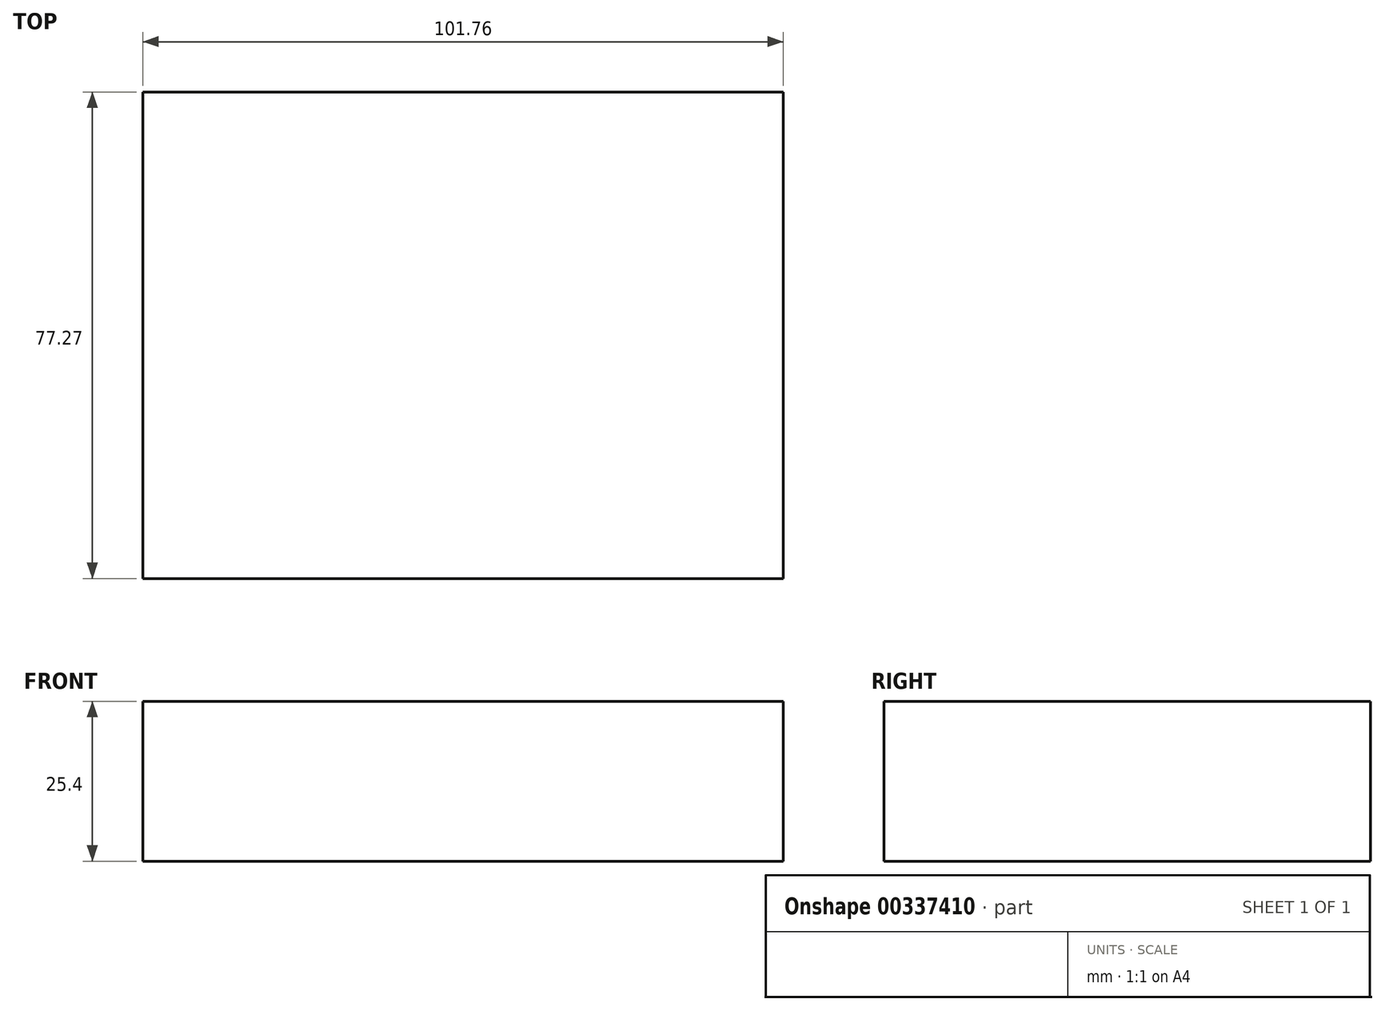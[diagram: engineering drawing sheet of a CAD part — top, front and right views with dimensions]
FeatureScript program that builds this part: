
annotation { "Feature Type Name" : "Feature", "Feature Type Description" : "" }
export const myFeature = defineFeature(function(context is Context, id is Id, definition is map)
    precondition{}
    {
        {
            var Q0;
            Q0=qCreatedBy(makeId("Top.planeOp"),FACE);
            var sketch = newSketch(context, id + "F0", { "sketchPlane" : qUnion([Q0])});
            skLineSegment(sketch, "E0.bottom", {"start": v(0, 0) * mm, "end": v(40.8, 0) * mm});
            skLineSegment(sketch, "E0.top", {"start": v(0, 0) * mm, "end": v(40.8, 0) * mm});
            skLineSegment(sketch, "E0.left", {"start": v(0, 0) * mm, "end": v(0, 0) * mm});
            skLineSegment(sketch, "E0.right", {"start": v(40.8, 0) * mm, "end": v(40.8, 0) * mm});
            skLineSegment(sketch, "E1.bottom", {"start": v(-47.1, 31.49) * mm, "end": v(54.65, 31.49) * mm});
            skLineSegment(sketch, "E1.top", {"start": v(-47.1, -45.78) * mm, "end": v(54.65, -45.78) * mm});
            skLineSegment(sketch, "E1.left", {"start": v(-47.1, 31.49) * mm, "end": v(-47.1, -45.78) * mm});
            skLineSegment(sketch, "E1.right", {"start": v(54.65, 31.49) * mm, "end": v(54.65, -45.78) * mm});
            skSolve(sketch);
        }
        {
            var Q0;
            Q0=makeQuery(id+"F0.imprint","IMPRINT",FACE,{"disambiguationData":[TD([[makeQuery(id+"F0.imprint","IMPRINT",EDGE,{"derivedFrom":sQuery(id+"F0.wireOp",EDGE,"E1.bottom")}),-1.0]])]});
            extrude(context, id + "F1", {"entities" : qUnion([Q0]), "depth" : 25.4 * mm});
        }
    });
